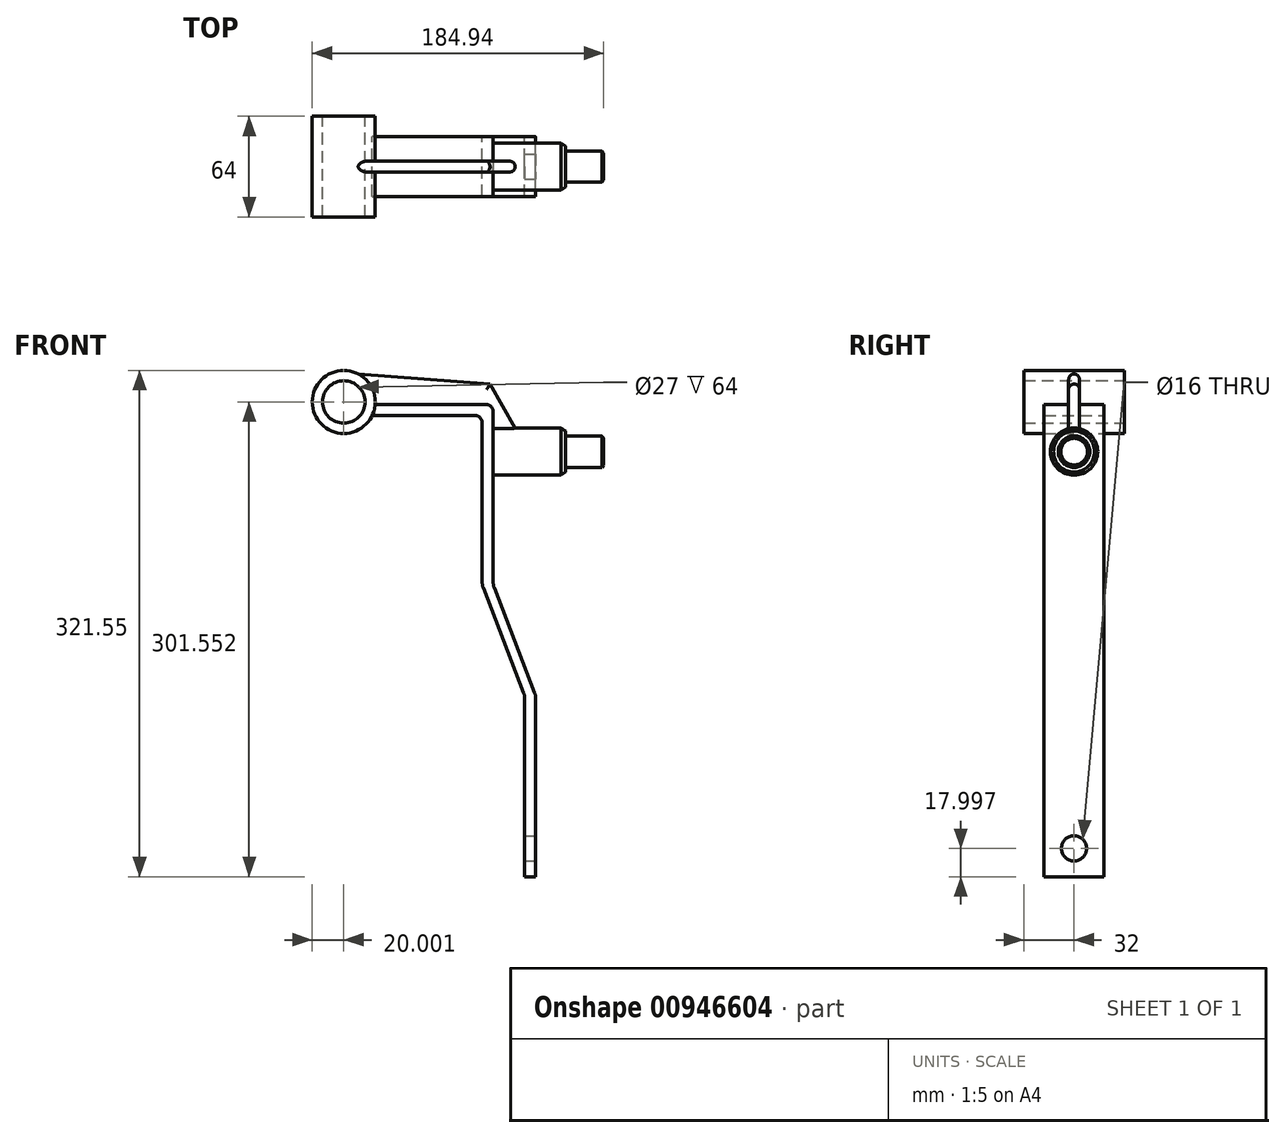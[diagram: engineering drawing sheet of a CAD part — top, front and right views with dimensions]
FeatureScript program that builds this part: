
annotation { "Feature Type Name" : "Feature", "Feature Type Description" : "" }
export const myFeature = defineFeature(function(context is Context, id is Id, definition is map)
    precondition{}
    {
        {
            var Q0;
            Q0=qCreatedBy(makeId("Front.planeOp"),FACE);
            var sketch = newSketch(context, id + "F0", { "sketchPlane" : qUnion([Q0])});
            skLineSegment(sketch, "E0", {"start": v(0, -214.98) * mm, "end": v(0, -101.85) * mm});
            skLineSegment(sketch, "E1", {"start": v(-0.67, -98.25) * mm, "end": v(-26.33, -31.72) * mm});
            skLineSegment(sketch, "E2", {"start": v(-27, -28.12) * mm, "end": v(-27, 80.02) * mm});
            skLineSegment(sketch, "E3", {"start": v(-32, 85.02) * mm, "end": v(-102, 85.02) * mm});
            skLineSegment(sketch, "E4", {"start": v(0, -214.98) * mm, "end": v(-7, -214.98) * mm});
            skLineSegment(sketch, "E5", {"start": v(-7, -214.98) * mm, "end": v(-7, -101.85) * mm});
            skLineSegment(sketch, "E6", {"start": v(-7.67, -98.25) * mm, "end": v(-33.33, -31.72) * mm});
            skLineSegment(sketch, "E7", {"start": v(-34, -28.12) * mm, "end": v(-34, 73.02) * mm});
            skCircle(sketch, "E8", {"center": v(-121.94, 86.57) * mm, "radius": 13.5 * mm});
            skArc(sketch, "E9", {"start": v(-102, 85.02) * mm, "mid": v(-141.27, 91.71) * mm, "end": v(-103.86, 78.02) * mm});
            skLineSegment(sketch, "E10", {"start": v(-39, 78.02) * mm, "end": v(-103.86, 78.02) * mm});
            skPoint(sketch, "E11.visualSharp", {"position": v(-27, -29.98) * mm});
            skArc(sketch, "E11.filletArc", {"start": v(-27, -28.12) * mm, "mid": v(-26.83, -29.95) * mm, "end": v(-26.33, -31.72) * mm});
            skPoint(sketch, "E12.visualSharp", {"position": v(-34, -29.98) * mm});
            skArc(sketch, "E12.filletArc", {"start": v(-34, -28.12) * mm, "mid": v(-33.83, -29.95) * mm, "end": v(-33.33, -31.72) * mm});
            skPoint(sketch, "E13.visualSharp", {"position": v(-7, -99.98) * mm});
            skArc(sketch, "E13.filletArc", {"start": v(-7, -101.85) * mm, "mid": v(-7.17, -100.01) * mm, "end": v(-7.67, -98.25) * mm});
            skPoint(sketch, "E14.visualSharp", {"position": v(0, -99.98) * mm});
            skArc(sketch, "E14.filletArc", {"start": v(0, -101.85) * mm, "mid": v(-0.17, -100.01) * mm, "end": v(-0.67, -98.25) * mm});
            skPoint(sketch, "E15.visualSharp", {"position": v(-27, 85.02) * mm});
            skArc(sketch, "E15.filletArc", {"start": v(-27, 80.02) * mm, "mid": v(-28.46, 83.55) * mm, "end": v(-32, 85.02) * mm});
            skPoint(sketch, "E16.visualSharp", {"position": v(-34, 78.02) * mm});
            skArc(sketch, "E16.filletArc", {"start": v(-34, 73.02) * mm, "mid": v(-35.46, 76.55) * mm, "end": v(-39, 78.02) * mm});
            skSolve(sketch);
        }
        {
            var Q0;
            Q0 = qSketchRegion(id + "F0", true);
            extrude(context, id + "F1", {"entities" : qUnion([Q0]), "depth" : 64 * mm, "offsetDistance" : 25 * mm});
        }
        {
            var Q0;
            Q0=makeQuery(id+"F1.opExtrude","SWEPT_FACE",FACE,{"disambiguationData":[OSD([sQuery(id+"F0.wireOp",EDGE,"E3")])]});
            var sketch = newSketch(context, id + "F2", { "sketchPlane" : qUnion([Q0])});
            skLineSegment(sketch, "E17.bottom", {"start": v(-102, 0) * mm, "end": v(0, 0) * mm});
            skLineSegment(sketch, "E17.top", {"start": v(-102, -13) * mm, "end": v(0, -13) * mm});
            skLineSegment(sketch, "E17.left", {"start": v(-102, 0) * mm, "end": v(-102, -13) * mm});
            skLineSegment(sketch, "E17.right", {"start": v(0, 0) * mm, "end": v(0, -13) * mm});
            skLineSegment(sketch, "E18.bottom", {"start": v(-102, -64) * mm, "end": v(0, -64) * mm});
            skLineSegment(sketch, "E18.top", {"start": v(-102, -51) * mm, "end": v(0, -51) * mm});
            skLineSegment(sketch, "E18.left", {"start": v(-102, -64) * mm, "end": v(-102, -51) * mm});
            skLineSegment(sketch, "E18.right", {"start": v(0, -64) * mm, "end": v(0, -51) * mm});
            skSolve(sketch);
        }
        {
            var Q0;
            Q0 = qSketchRegion(id + "F2", true);
            extrude(context, id + "F3", {"entities" : qUnion([Q0]), "operationType" : NewBodyOperationType.REMOVE, "oppositeDirection" : true, "depth" : 400 * mm, "offsetDistance" : 25 * mm});
        }
        {
            var Q0;
            Q0=makeQuery(id+"F1.opExtrude","CAP_FACE",FACE,{"disambiguationData":[OSD([sQuery(id+"F0.wireOp",EDGE,"E0"),sQuery(id+"F0.wireOp",EDGE,"E1"),sQuery(id+"F0.wireOp",EDGE,"E2"),sQuery(id+"F0.wireOp",EDGE,"E3"),sQuery(id+"F0.wireOp",EDGE,"E4"),sQuery(id+"F0.wireOp",EDGE,"E5"),sQuery(id+"F0.wireOp",EDGE,"E6"),sQuery(id+"F0.wireOp",EDGE,"E7"),sQuery(id+"F0.wireOp",EDGE,"E8"),sQuery(id+"F0.wireOp",EDGE,"E9"),sQuery(id+"F0.wireOp",EDGE,"E10"),sQuery(id+"F0.wireOp",EDGE,"E11.filletArc"),sQuery(id+"F0.wireOp",EDGE,"E12.filletArc"),sQuery(id+"F0.wireOp",EDGE,"E13.filletArc"),sQuery(id+"F0.wireOp",EDGE,"E14.filletArc"),sQuery(id+"F0.wireOp",EDGE,"E15.filletArc"),sQuery(id+"F0.wireOp",EDGE,"E16.filletArc")])],"isStart":true});
            var sketch = newSketch(context, id + "F4", { "sketchPlane" : qUnion([Q0])});
            skLineSegment(sketch, "E19", {"start": v(102, 85.02) * mm, "end": v(102, 78.02) * mm});
            skLineSegment(sketch, "E20", {"start": v(102, 78.02) * mm, "end": v(103.86, 78.02) * mm});
            skArc(sketch, "E21", {"start": v(102, 85.02) * mm, "mid": v(102.61, 81.43) * mm, "end": v(103.86, 78.02) * mm});
            skSolve(sketch);
        }
        {
            var Q0;
            Q0 = qSketchRegion(id + "F4", true);
            extrude(context, id + "F5", {"entities" : qUnion([Q0]), "operationType" : NewBodyOperationType.REMOVE, "oppositeDirection" : true, "depth" : 13 * mm, "offsetDistance" : 25 * mm});
        }
        {
            var Q0;
            Q0=makeQuery(id+"F1.opExtrude","CAP_FACE",FACE,{"disambiguationData":[OSD([sQuery(id+"F0.wireOp",EDGE,"E0"),sQuery(id+"F0.wireOp",EDGE,"E1"),sQuery(id+"F0.wireOp",EDGE,"E2"),sQuery(id+"F0.wireOp",EDGE,"E3"),sQuery(id+"F0.wireOp",EDGE,"E4"),sQuery(id+"F0.wireOp",EDGE,"E5"),sQuery(id+"F0.wireOp",EDGE,"E6"),sQuery(id+"F0.wireOp",EDGE,"E7"),sQuery(id+"F0.wireOp",EDGE,"E8"),sQuery(id+"F0.wireOp",EDGE,"E9"),sQuery(id+"F0.wireOp",EDGE,"E10"),sQuery(id+"F0.wireOp",EDGE,"E11.filletArc"),sQuery(id+"F0.wireOp",EDGE,"E12.filletArc"),sQuery(id+"F0.wireOp",EDGE,"E13.filletArc"),sQuery(id+"F0.wireOp",EDGE,"E14.filletArc"),sQuery(id+"F0.wireOp",EDGE,"E15.filletArc"),sQuery(id+"F0.wireOp",EDGE,"E16.filletArc")])],"isStart":false});
            var sketch = newSketch(context, id + "F6", { "sketchPlane" : qUnion([Q0])});
            skLineSegment(sketch, "E22", {"start": v(-102, 85.02) * mm, "end": v(-102, 78.02) * mm});
            skLineSegment(sketch, "E23", {"start": v(-102, 78.02) * mm, "end": v(-103.86, 78.02) * mm});
            skArc(sketch, "E24", {"start": v(-103.86, 78.02) * mm, "mid": v(-102.61, 81.43) * mm, "end": v(-102, 85.02) * mm});
            skSolve(sketch);
        }
        {
            var Q0;
            Q0 = qSketchRegion(id + "F6", true);
            extrude(context, id + "F7", {"entities" : qUnion([Q0]), "operationType" : NewBodyOperationType.REMOVE, "oppositeDirection" : true, "depth" : 13 * mm, "offsetDistance" : 25 * mm});
        }
        {
            var Q0;
            Q0=makeQuery(id+"F1.opExtrude","SWEPT_FACE",FACE,{"disambiguationData":[OSD([sQuery(id+"F0.wireOp",EDGE,"E2")])]});
            var sketch = newSketch(context, id + "F8", { "sketchPlane" : qUnion([Q0])});
            skCircle(sketch, "E25", {"center": v(-32, 55.02) * mm, "radius": 15 * mm});
            skPoint(sketch, "E25.centerSnap0", {"position": v(-32, -28.12) * mm});
            skSolve(sketch);
        }
        {
            var Q0;
            Q0 = qSketchRegion(id + "F8", true);
            extrude(context, id + "F9", {"entities" : qUnion([Q0]), "operationType" : NewBodyOperationType.ADD, "depth" : 43 * mm, "offsetDistance" : 25 * mm});
        }
        {
            var Q0;
            Q0 = qBodyType(qCreatedBy(id + "F8" ,EDGE), BodyType.WIRE);
            cPlane(context, id + "F10", {"entities" : qUnion([Q0]), "cplaneType" : CPlaneType.LINE_ANGLE, "offset" : 25 * mm, "angle" : 0 * degree, "width" : 150 * mm, "height" : 150 * mm});
        }
        {
            var Q0;
            Q0=qCreatedBy(id+"F10.planeOp",FACE);
            var sketch = newSketch(context, id + "F11", { "sketchPlane" : qUnion([Q0])});
            skLineSegment(sketch, "E26", {"start": v(-16, 70.02) * mm, "end": v(-16, 55.02) * mm});
            skLineSegment(sketch, "E27", {"start": v(-16, 70.02) * mm, "end": v(-19, 68.02) * mm});
            skLineSegment(sketch, "E28", {"start": v(-19, 68.02) * mm, "end": v(-19, 65.02) * mm});
            skLineSegment(sketch, "E29", {"start": v(-19, 65.02) * mm, "end": v(-42, 65.02) * mm});
            skLineSegment(sketch, "E30", {"start": v(-42, 65.02) * mm, "end": v(-43, 63.52) * mm});
            skLineSegment(sketch, "E31", {"start": v(-43, 63.52) * mm, "end": v(-43, 55.02) * mm});
            skLineSegment(sketch, "E32", {"start": v(-16, 55.02) * mm, "end": v(-43, 55.02) * mm});
            skSolve(sketch);
        }
        {
            var Q0;
            Q0 = qSketchRegion(id + "F11", true);
            var Q1;
            Q1=sQuery(id+"F11.wireOp",EDGE,"E32");
            revolve(context, id + "F12", {"operationType" : NewBodyOperationType.ADD, "surfaceOperationType" : NewSurfaceOperationType.NEW, "entities" : qUnion([Q0]), "axis" : qUnion([Q1]), "revolveType" : RevolveType.FULL});
        }
        {
            var Q0;
            Q0=qCreatedBy(id+"F10.planeOp",FACE);
            var sketch = newSketch(context, id + "F13", { "sketchPlane" : qUnion([Q0])});
            skArc(sketch, "E33", {"start": v(113.06, 104.4) * mm, "mid": v(104.6, 96.39) * mm, "end": v(102.06, 85.02) * mm});
            skLineSegment(sketch, "E34", {"start": v(102.06, 85.02) * mm, "end": v(32, 85.02) * mm});
            skLineSegment(sketch, "E35", {"start": v(27, 80.02) * mm, "end": v(27, 70.02) * mm});
            skLineSegment(sketch, "E36", {"start": v(13.06, 70.02) * mm, "end": v(29.06, 97.9) * mm});
            skLineSegment(sketch, "E37", {"start": v(29.06, 97.9) * mm, "end": v(113.06, 104.4) * mm});
            skPoint(sketch, "E38.visualSharp", {"position": v(27, 85.02) * mm});
            skArc(sketch, "E38.filletArc", {"start": v(32, 85.02) * mm, "mid": v(28.46, 83.55) * mm, "end": v(27, 80.02) * mm});
            skLineSegment(sketch, "E39", {"start": v(13.06, 70.02) * mm, "end": v(10.79, 66.06) * mm});
            skLineSegment(sketch, "E40", {"start": v(10.79, 66.06) * mm, "end": v(27, 66.06) * mm});
            skLineSegment(sketch, "E41", {"start": v(27, 66.06) * mm, "end": v(27, 70.02) * mm});
            skSolve(sketch);
        }
        {
            var Q0;
            Q0 = qSketchRegion(id + "F13", true);
            extrude(context, id + "F14", {"entities" : qUnion([Q0]), "operationType" : NewBodyOperationType.ADD, "depth" : 3.5 * mm, "offsetDistance" : 25 * mm, "hasSecondDirection" : true, "secondDirectionOppositeDirection" : true, "secondDirectionDepth" : 3.5 * mm});
        }
        {
            var Q0;
            Q0=makeQuery(id+"F1.opExtrude","SWEPT_FACE",FACE,{"disambiguationData":[OSD([sQuery(id+"F0.wireOp",EDGE,"E0")])]});
            var sketch = newSketch(context, id + "F15", { "sketchPlane" : qUnion([Q0])});
            skCircle(sketch, "E42", {"center": v(-32, -196.98) * mm, "radius": 8 * mm});
            skPoint(sketch, "E42.centerSnap0", {"position": v(-32, -214.98) * mm});
            skSolve(sketch);
        }
        {
            var Q0;
            Q0 = qSketchRegion(id + "F15", true);
            extrude(context, id + "F16", {"entities" : qUnion([Q0]), "operationType" : NewBodyOperationType.REMOVE, "oppositeDirection" : true, "depth" : 25 * mm, "offsetDistance" : 25 * mm});
        }
        {
            var Q0;
            Q0=makeQuery(id+"F14.opExtrude","CAP_EDGE",EDGE,{"disambiguationData":[OSD([sQuery(id+"F13.wireOp",EDGE,"E37")])],"isStart":true});
            var Q1;
            Q1=makeQuery(id+"F14.opExtrude","CAP_EDGE",EDGE,{"disambiguationData":[OSD([sQuery(id+"F13.wireOp",EDGE,"E37")])],"isStart":false});
            var Q2;
            Q2=makeQuery(id+"F14.opExtrude","CAP_EDGE",EDGE,{"disambiguationData":[OSD([sQuery(id+"F13.wireOp",EDGE,"E36"),sQuery(id+"F13.wireOp",EDGE,"E39")])],"isStart":true});
            var Q3;
            Q3=makeQuery(id+"F14.opExtrude","CAP_EDGE",EDGE,{"disambiguationData":[OSD([sQuery(id+"F13.wireOp",EDGE,"E36"),sQuery(id+"F13.wireOp",EDGE,"E39")])],"isStart":false});
            fillet(context, id + "F17", {"entities" : qUnion([Q0, Q1, Q2, Q3]), "radius" : 3.5 * mm, "tangentPropagation" : true, "allowEdgeOverflow" : false});
        }
    });
